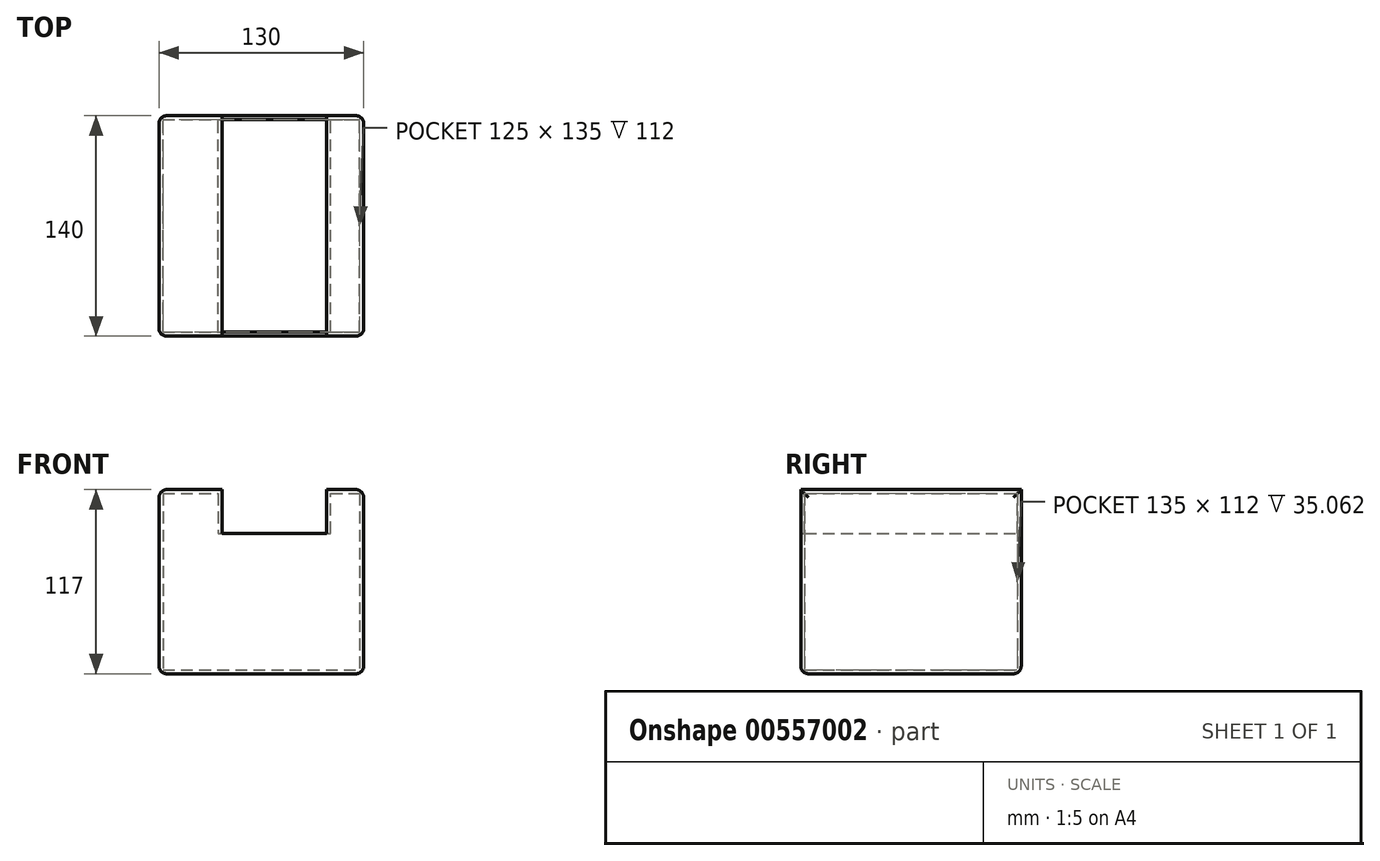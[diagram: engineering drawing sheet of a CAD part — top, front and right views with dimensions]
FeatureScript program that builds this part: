
annotation { "Feature Type Name" : "Feature", "Feature Type Description" : "" }
export const myFeature = defineFeature(function(context is Context, id is Id, definition is map)
    precondition{}
    {
        {
            var Q0;
            Q0=qCreatedBy(makeId("Front.planeOp"),FACE);
            var sketch = newSketch(context, id + "F0", { "sketchPlane" : qUnion([Q0])});
            skLineSegment(sketch, "E0.top", {"start": v(-68.4, -74.04) * mm, "end": v(61.6, -74.04) * mm});
            skLineSegment(sketch, "E0.left", {"start": v(-68.4, 42.96) * mm, "end": v(-68.4, -74.04) * mm});
            skLineSegment(sketch, "E0.right", {"start": v(61.6, 42.96) * mm, "end": v(61.6, -74.04) * mm});
            skLineSegment(sketch, "E1", {"start": v(-68.4, 42.96) * mm, "end": v(-28.34, 42.96) * mm});
            skLineSegment(sketch, "E2", {"start": v(-28.34, 42.96) * mm, "end": v(-28.34, 15.16) * mm});
            skLineSegment(sketch, "E3", {"start": v(-28.34, 15.16) * mm, "end": v(38.16, 15.16) * mm});
            skLineSegment(sketch, "E4", {"start": v(38.16, 15.16) * mm, "end": v(38.16, 42.96) * mm});
            skLineSegment(sketch, "E5", {"start": v(38.16, 42.96) * mm, "end": v(61.6, 42.96) * mm});
            skSolve(sketch);
        }
        {
            var Q0;
            Q0 = qSketchRegion(id + "F0", true);
            extrude(context, id + "F1", {"entities" : qUnion([Q0]), "depth" : 140 * mm, "offsetDistance" : 25 * mm});
        }
        {
            var Q0;
            Q0=makeQuery(id+"F1.opExtrude","SWEPT_FACE",FACE,{"disambiguationData":[OSD([sQuery(id+"F0.wireOp",EDGE,"E3")])]});
            shell(context, id + "F2", {"entities" : qUnion([Q0]), "thickness" : 2.5 * mm});
        }
        {
            var Q0;
            Q0=makeQuery(id+"F1.opExtrude","SWEPT_FACE",FACE,{"disambiguationData":[OSD([sQuery(id+"F0.wireOp",EDGE,"E0.left")])]});
            var Q1;
            Q1=makeQuery(id+"F1.opExtrude","SWEPT_FACE",FACE,{"disambiguationData":[OSD([sQuery(id+"F0.wireOp",EDGE,"E0.right")])]});
            var Q2;
            Q2=makeQuery(id+"F1.opExtrude","SWEPT_FACE",FACE,{"disambiguationData":[OSD([sQuery(id+"F0.wireOp",EDGE,"E0.top")])]});
            fillet(context, id + "F3", {"entities" : qUnion([Q0, Q1, Q2]), "radius" : 5 * mm, "tangentPropagation" : true, "allowEdgeOverflow" : false});
        }
    });
